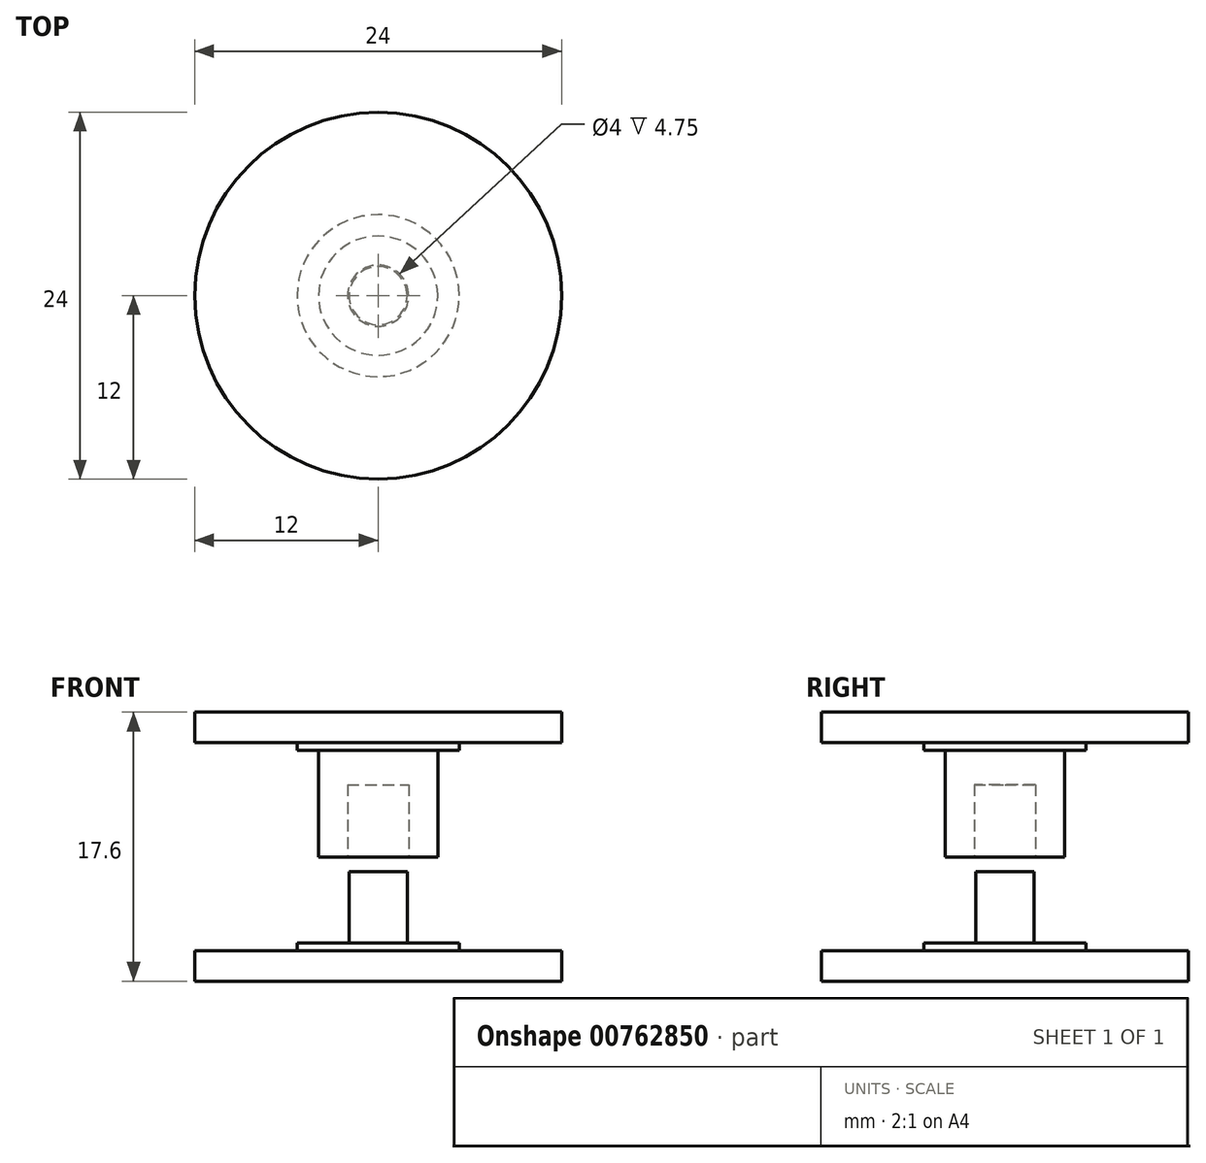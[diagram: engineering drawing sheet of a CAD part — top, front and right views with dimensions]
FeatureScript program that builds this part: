
annotation { "Feature Type Name" : "Feature", "Feature Type Description" : "" }
export const myFeature = defineFeature(function(context is Context, id is Id, definition is map)
    precondition{}
    {
        {
            var Q0;
            Q0=qCreatedBy(makeId("Front.planeOp"),FACE);
            var sketch = newSketch(context, id + "F0", { "sketchPlane" : qUnion([Q0])});
            skLineSegment(sketch, "E0", {"start": v(12, 39.56) * mm, "end": v(12, 37.56) * mm});
            skLineSegment(sketch, "E1", {"start": v(12, 37.56) * mm, "end": v(5.3, 37.56) * mm});
            skLineSegment(sketch, "E2", {"start": v(5.3, 37.56) * mm, "end": v(5.3, 37.06) * mm});
            skLineSegment(sketch, "E3", {"start": v(5.3, 37.06) * mm, "end": v(3.9, 37.06) * mm});
            skLineSegment(sketch, "E4", {"start": v(3.9, 37.06) * mm, "end": v(3.9, 30.06) * mm});
            skLineSegment(sketch, "E5", {"start": v(3.9, 30.06) * mm, "end": v(2, 30.06) * mm});
            skLineSegment(sketch, "E6", {"start": v(0, 34.81) * mm, "end": v(0, 38.35) * mm});
            skLineSegment(sketch, "E7", {"start": v(2, 30.06) * mm, "end": v(2, 34.81) * mm});
            skLineSegment(sketch, "E8", {"start": v(2, 34.81) * mm, "end": v(0, 34.81) * mm});
            skPoint(sketch, "E9.orphan", {"position": v(3.9, 30.06) * mm});
            skPoint(sketch, "E10.orphan", {"position": v(0, 39.56) * mm});
            skLineSegment(sketch, "E11", {"start": v(12, 39.56) * mm, "end": v(0, 39.56) * mm});
            skLineSegment(sketch, "E12", {"start": v(0, 39.56) * mm, "end": v(0, 38.35) * mm});
            skPoint(sketch, "E13.center.orphan", {"position": v(0, 98.35) * mm});
            skLineSegment(sketch, "E14", {"start": v(0, 29.1) * mm, "end": v(1.9, 29.1) * mm});
            skLineSegment(sketch, "E15", {"start": v(1.9, 29.1) * mm, "end": v(1.9, 24.46) * mm});
            skLineSegment(sketch, "E16", {"start": v(1.9, 24.46) * mm, "end": v(5.3, 24.46) * mm});
            skLineSegment(sketch, "E17", {"start": v(5.3, 24.46) * mm, "end": v(5.3, 23.96) * mm});
            skLineSegment(sketch, "E18", {"start": v(5.3, 23.96) * mm, "end": v(12, 23.96) * mm});
            skLineSegment(sketch, "E19", {"start": v(12, 23.96) * mm, "end": v(12, 21.96) * mm});
            skLineSegment(sketch, "E20", {"start": v(12, 21.96) * mm, "end": v(0, 21.96) * mm});
            skLineSegment(sketch, "E21", {"start": v(0, 21.96) * mm, "end": v(0, 29.1) * mm});
            skLineSegment(sketch, "E22", {"start": v(0, 69.31) * mm, "end": v(0, -64.18) * mm, "construction": true});
            skSolve(sketch);
        }
        {
            var Q0;
            Q0=makeQuery(id+"F0.imprint","IMPRINT",FACE,{"disambiguationData":[TD([[makeQuery(id+"F0.imprint","IMPRINT",EDGE,{"derivedFrom":sQuery(id+"F0.wireOp",EDGE,"E0")}),-1.0]])]});
            var Q1;
            Q1=sQuery(id+"F0.wireOp",EDGE,"E6");
            revolve(context, id + "F1", {"entities" : qUnion([Q0]), "axis" : qUnion([Q1]), "revolveType" : RevolveType.FULL});
        }
        {
            var Q0;
            Q0=qSketchRegion(id+"F0",true);
            var Q1;
            Q1=makeQuery(id+"F1.opRevolve","SWEPT_FACE",FACE,{"disambiguationData":[OSD([sQuery(id+"F0.wireOp",EDGE,"E4")])]});
            revolve(context, id + "F2", {"operationType" : NewBodyOperationType.ADD, "surfaceOperationType" : NewSurfaceOperationType.NEW, "entities" : qUnion([Q0]), "axis" : qUnion([Q1]), "revolveType" : RevolveType.FULL});
        }
    });
